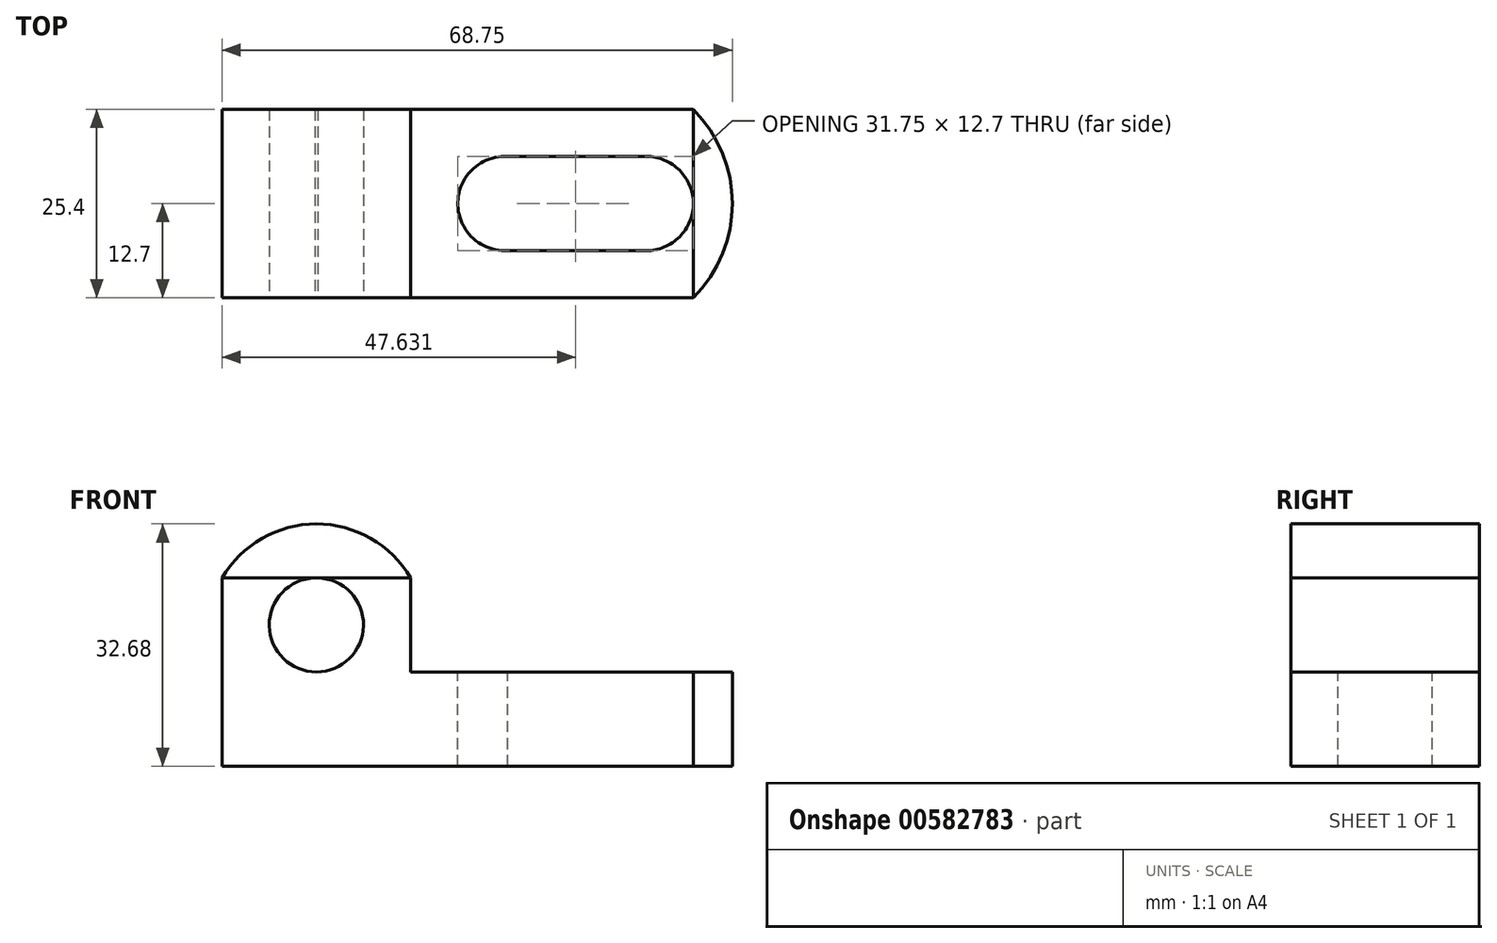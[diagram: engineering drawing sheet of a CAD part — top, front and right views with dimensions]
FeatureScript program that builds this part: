
annotation { "Feature Type Name" : "Feature", "Feature Type Description" : "" }
export const myFeature = defineFeature(function(context is Context, id is Id, definition is map)
    precondition{}
    {
        {
            var Q0;
            Q0=qCreatedBy(makeId("Front.planeOp"),FACE);
            var sketch = newSketch(context, id + "F0", { "sketchPlane" : qUnion([Q0])});
            skLineSegment(sketch, "E0", {"start": v(-66.94, 47.18) * mm, "end": v(-66.93, 21.78) * mm});
            skLineSegment(sketch, "E1", {"start": v(-66.93, 21.78) * mm, "end": v(-3.43, 21.8) * mm});
            skLineSegment(sketch, "E2", {"start": v(-3.43, 21.8) * mm, "end": v(-3.44, 34.5) * mm});
            skLineSegment(sketch, "E3", {"start": v(-3.44, 34.5) * mm, "end": v(-41.54, 34.5) * mm});
            skLineSegment(sketch, "E4", {"start": v(-41.54, 34.5) * mm, "end": v(-41.54, 47.2) * mm});
            skLineSegment(sketch, "E5", {"start": v(-41.54, 47.2) * mm, "end": v(-66.94, 47.18) * mm});
            skSolve(sketch);
        }
        {
            var Q0;
            Q0 = qSketchRegion(id + "F0", true);
            extrude(context, id + "F1", {"entities" : qUnion([Q0]), "depth" : 25.4 * mm, "offsetDistance" : 25.4 * mm});
        }
        {
            var Q0;
            Q0=makeQuery(id+"F1.opExtrude","SWEPT_FACE",FACE,{"disambiguationData":[OSD([sQuery(id+"F0.wireOp",EDGE,"E3")])]});
            var sketch = newSketch(context, id + "F2", { "sketchPlane" : qUnion([Q0])});
            skCircle(sketch, "E6", {"center": v(-28.84, -12.7) * mm, "radius": 6.35 * mm});
            skCircle(sketch, "E7", {"center": v(-9.79, -12.7) * mm, "radius": 6.35 * mm});
            skLineSegment(sketch, "E8", {"start": v(-28.46, -6.36) * mm, "end": v(-9.79, -6.35) * mm});
            skLineSegment(sketch, "E9", {"start": v(-9.79, -6.35) * mm, "end": v(-9.79, -19.05) * mm});
            skLineSegment(sketch, "E10", {"start": v(-9.79, -19.05) * mm, "end": v(-28.84, -19.05) * mm});
            skLineSegment(sketch, "E11", {"start": v(-28.84, -19.05) * mm, "end": v(-28.46, -6.36) * mm});
            skSolve(sketch);
        }
        {
            var Q0;
            Q0 = qSketchRegion(id + "F2", true);
            extrude(context, id + "F3", {"entities" : qUnion([Q0]), "operationType" : NewBodyOperationType.REMOVE, "oppositeDirection" : true, "depth" : 12.7 * mm, "offsetDistance" : 25.4 * mm});
        }
        {
            var Q0;
            Q0=makeQuery(id+"F1.opExtrude","SWEPT_FACE",FACE,{"disambiguationData":[OSD([sQuery(id+"F0.wireOp",EDGE,"E3")])]});
            var sketch = newSketch(context, id + "F4", { "sketchPlane" : qUnion([Q0])});
            skArc(sketch, "E12", {"start": v(-3.44, -25.4) * mm, "mid": v(1.81, -12.7) * mm, "end": v(-3.44, 0) * mm});
            skLineSegment(sketch, "E13", {"start": v(-3.44, 0) * mm, "end": v(-3.44, -25.4) * mm});
            skSolve(sketch);
        }
        {
            var Q0;
            Q0 = qSketchRegion(id + "F4", true);
            extrude(context, id + "F5", {"entities" : qUnion([Q0]), "oppositeDirection" : true, "depth" : 12.7 * mm, "offsetDistance" : 25.4 * mm});
        }
        {
            var Q0;
            Q0=makeQuery(id+"F1.opExtrude","CAP_FACE",FACE,{"disambiguationData":[OSD([sQuery(id+"F0.wireOp",EDGE,"E0"),sQuery(id+"F0.wireOp",EDGE,"E1"),sQuery(id+"F0.wireOp",EDGE,"E2"),sQuery(id+"F0.wireOp",EDGE,"E3"),sQuery(id+"F0.wireOp",EDGE,"E4"),sQuery(id+"F0.wireOp",EDGE,"E5")])],"isStart":false});
            var sketch = newSketch(context, id + "F6", { "sketchPlane" : qUnion([Q0])});
            skCircle(sketch, "E14", {"center": v(-54.23, 40.84) * mm, "radius": 6.35 * mm});
            skSolve(sketch);
        }
        {
            var Q0;
            Q0 = qSketchRegion(id + "F6", true);
            extrude(context, id + "F7", {"entities" : qUnion([Q0]), "operationType" : NewBodyOperationType.REMOVE, "oppositeDirection" : true, "depth" : 25.4 * mm, "offsetDistance" : 25.4 * mm});
        }
        {
            var Q0;
            Q0=makeQuery(id+"F1.opExtrude","CAP_FACE",FACE,{"disambiguationData":[OSD([sQuery(id+"F0.wireOp",EDGE,"E0"),sQuery(id+"F0.wireOp",EDGE,"E1"),sQuery(id+"F0.wireOp",EDGE,"E2"),sQuery(id+"F0.wireOp",EDGE,"E3"),sQuery(id+"F0.wireOp",EDGE,"E4"),sQuery(id+"F0.wireOp",EDGE,"E5")])],"isStart":false});
            var sketch = newSketch(context, id + "F8", { "sketchPlane" : qUnion([Q0])});
            skArc(sketch, "E15", {"start": v(-41.54, 47.2) * mm, "mid": v(-54.24, 54.46) * mm, "end": v(-66.94, 47.18) * mm});
            skLineSegment(sketch, "E16", {"start": v(-66.94, 47.18) * mm, "end": v(-41.54, 47.2) * mm});
            skSolve(sketch);
        }
        {
            var Q0;
            Q0 = qSketchRegion(id + "F8", true);
            extrude(context, id + "F9", {"entities" : qUnion([Q0]), "oppositeDirection" : true, "depth" : 25.4 * mm, "offsetDistance" : 25.4 * mm});
        }
    });
